# Revit family: GNW_A3-Casement-Timber-4Lite-Trim-(NZ)
name_source: partatom
category: Windows
revit_build: Autodesk Revit 2016 (Build: 20150220_1215(x64)
units: mm (PartAtom-declared; Revit-internal decimal feet)

## family parameters
Always vertical = Yes
Cut with Voids When Loaded = No
Host = Wall
Room Calculation Point = No
Shared = No

## types (1)
- 1020 x 1200 Timber
    Architrave Thickness = 15 mm  [stored 0.0492126 ft]
    Architrave Width = 45 mm  [stored 0.147638 ft]
    CoverBd Thickness = 20 mm  [stored 0.0656168 ft]
    CoverBd Width = 90 mm  [stored 0.295276 ft]
    Default Sill Height = 800 mm  [stored 2.62467 ft]
    Frame Thickness = 32 mm  [stored 0.104987 ft]
    Height = 1200 mm
    Operation = DoublePanelVertical
    Rebate Thickness = 17 mm
    Rough Height = 1274 mm  [stored 4.17979 ft]
    Rough Width = 1094 mm
    Sash Thickness = 50 mm  [stored 0.164042 ft]
    Sill Thickness = 55 mm  [stored 0.180446 ft]
    Structural Tolerance = 5 mm  [stored 0.0164042 ft]
    Wall Closure = By host
    Width = 1020 mm  [stored 3.34646 ft]
    WithinWall = 0 mm  [stored 0 ft]

note: [stored X ft] marks values corroborated as IEEE doubles in the binary element streams (Revit-internal decimal feet)

## geometry (parser evidence)
native form markers: Sweep x2
no freeform markers — native parametric forms only
